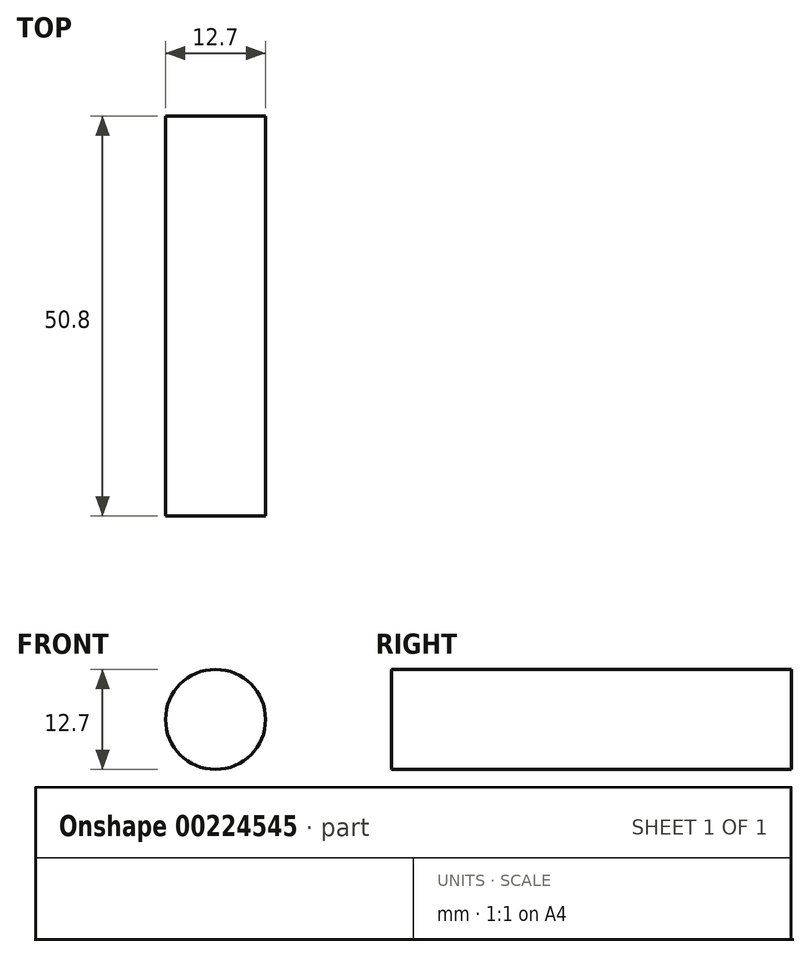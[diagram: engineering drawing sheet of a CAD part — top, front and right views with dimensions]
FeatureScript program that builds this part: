
annotation { "Feature Type Name" : "Feature", "Feature Type Description" : "" }
export const myFeature = defineFeature(function(context is Context, id is Id, definition is map)
    precondition{}
    {
        {
            var Q0;
            Q0=qCreatedBy(makeId("Front.planeOp"),FACE);
            var sketch = newSketch(context, id + "F0", { "sketchPlane" : qUnion([Q0])});
            skCircle(sketch, "E0", {"center": v(-41.81, 29.42) * mm, "radius": 6.35 * mm});
            skSolve(sketch);
        }
        {
            var Q0;
            Q0=makeQuery(id+"F0.imprint","IMPRINT",FACE,{"disambiguationData":[TD([[makeQuery(id+"F0.imprint","IMPRINT",EDGE,{"derivedFrom":sQuery(id+"F0.wireOp",EDGE,"E0")}),1.0]])]});
            extrude(context, id + "F1", {"entities" : qUnion([Q0]), "depth" : 50.8 * mm});
        }
    });
